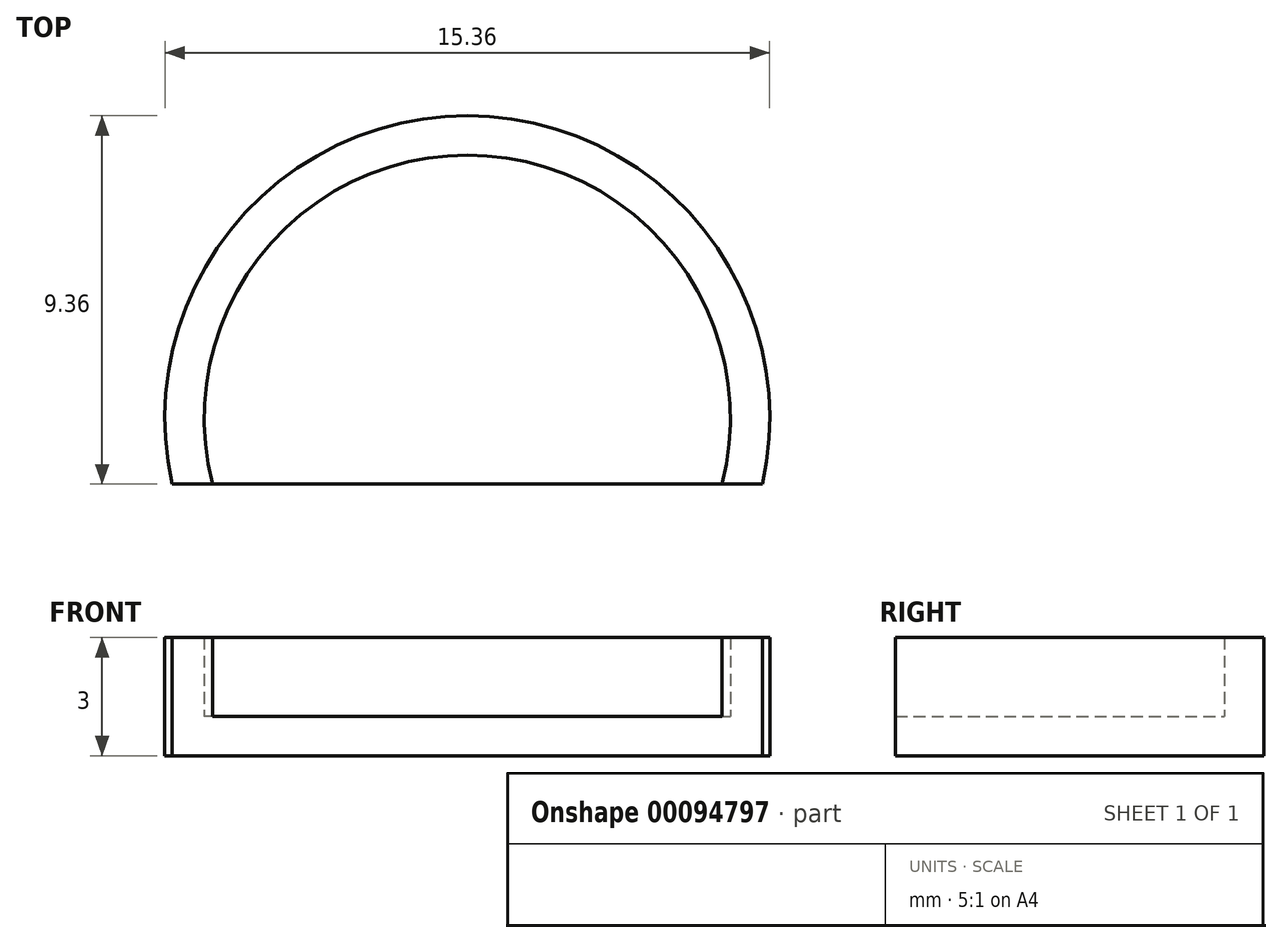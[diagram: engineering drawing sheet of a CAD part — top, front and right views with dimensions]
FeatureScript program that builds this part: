
annotation { "Feature Type Name" : "Feature", "Feature Type Description" : "" }
export const myFeature = defineFeature(function(context is Context, id is Id, definition is map)
    precondition{}
    {
        {
            var Q0;
            Q0=qCreatedBy(makeId("Top.planeOp"),FACE);
            var sketch = newSketch(context, id + "F2", { "sketchPlane" : qUnion([Q0])});
            skArc(sketch, "E0", {"start": v(7.5, 0) * mm, "mid": v(0, 9.36) * mm, "end": v(-7.5, 0) * mm});
            skLineSegment(sketch, "E1", {"start": v(-7.5, 0) * mm, "end": v(7.5, 0) * mm});
            skSolve(sketch);
        }
        {
            var Q0;
            Q0=makeQuery(id+"F2.imprint","IMPRINT",FACE,{"disambiguationData":[TD([[makeQuery(id+"F2.imprint","IMPRINT",EDGE,{"derivedFrom":sQuery(id+"F2.wireOp",EDGE,"E0")}),1.0]])]});
            extrude(context, id + "F0", {"entities" : qUnion([Q0]), "depth" : 3 * mm});
        }
        {
            var Q0;
            Q0=makeQuery(id+"F0.opExtrude","CAP_FACE",FACE,{"disambiguationData":[OSD([sQuery(id+"F2.wireOp",EDGE,"E0"),sQuery(id+"F2.wireOp",EDGE,"E1")])],"isStart":false});
            var Q1;
            Q1=makeQuery(id+"F0.opExtrude","SWEPT_FACE",FACE,{"disambiguationData":[OSD([sQuery(id+"F2.wireOp",EDGE,"E1")])]});
            shell(context, id + "F1", {"entities" : qUnion([Q0, Q1]), "thickness" : 1 * mm});
        }
    });
